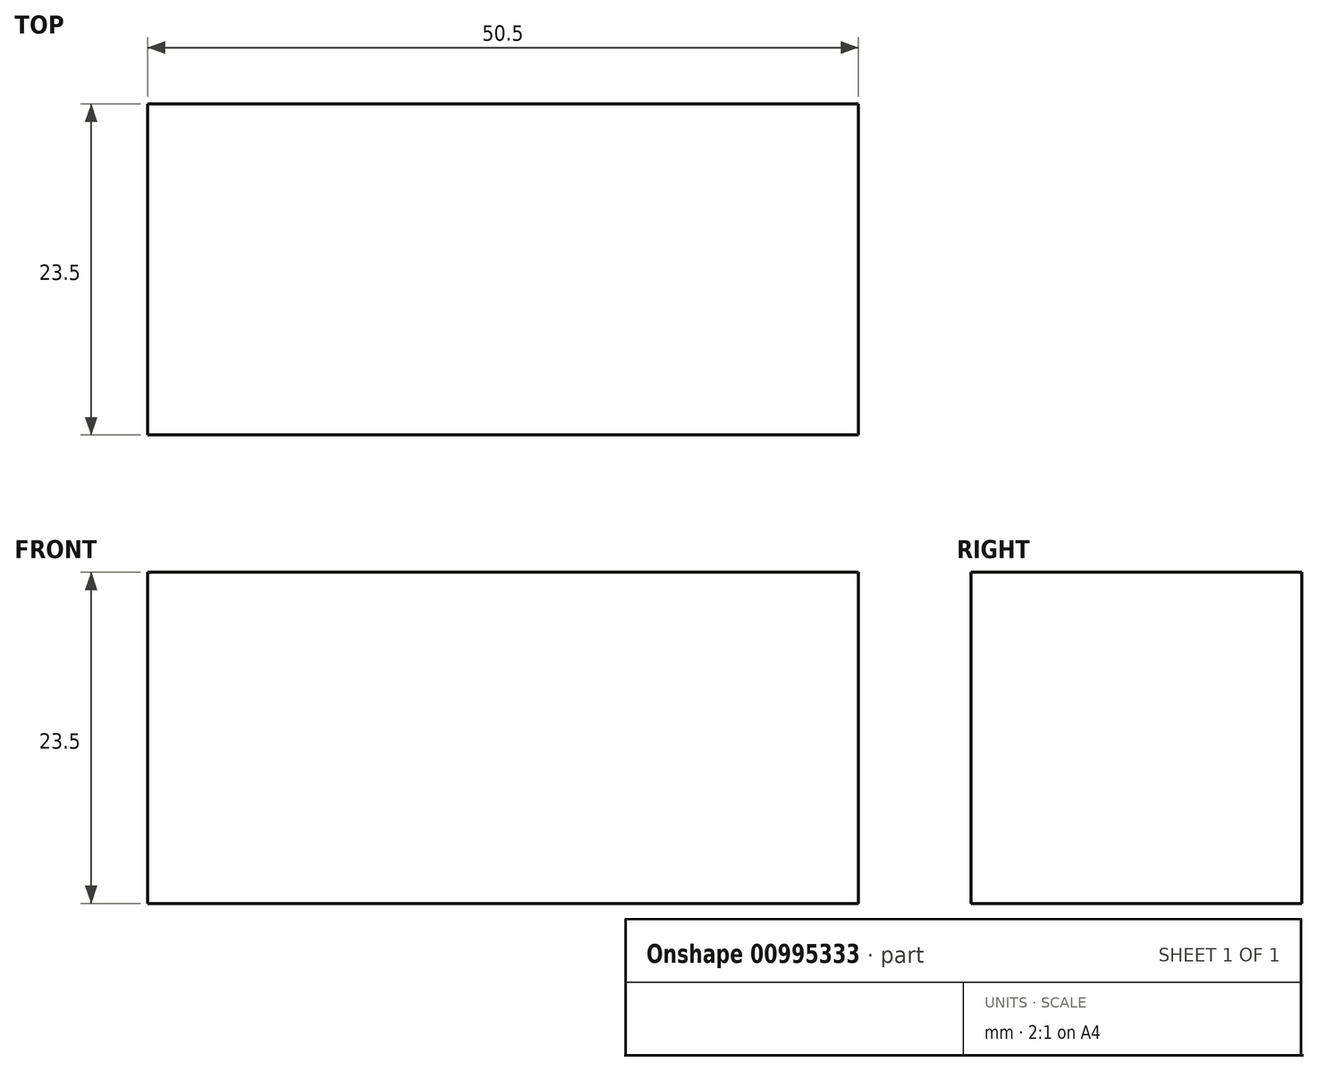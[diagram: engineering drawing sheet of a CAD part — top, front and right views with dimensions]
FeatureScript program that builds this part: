
annotation { "Feature Type Name" : "Feature", "Feature Type Description" : "" }
export const myFeature = defineFeature(function(context is Context, id is Id, definition is map)
    precondition{}
    {
        {
            var Q0;
            Q0=qCreatedBy(makeId("Top.planeOp"),FACE);
            var sketch = newSketch(context, id + "F0", { "sketchPlane" : qUnion([Q0])});
            skLineSegment(sketch, "E0.bottom", {"start": v(25.25, 11.75) * mm, "end": v(-25.25, 11.75) * mm});
            skLineSegment(sketch, "E0.top", {"start": v(25.25, -11.75) * mm, "end": v(-25.25, -11.75) * mm});
            skLineSegment(sketch, "E0.left", {"start": v(25.25, 11.75) * mm, "end": v(25.25, -11.75) * mm});
            skLineSegment(sketch, "E0.right", {"start": v(-25.25, 11.75) * mm, "end": v(-25.25, -11.75) * mm});
            skPoint(sketch, "E0.middle", {"position": v(0, 0) * mm});
            skSolve(sketch);
        }
        {
            var Q0;
            Q0 = qSketchRegion(id + "F0", true);
            extrude(context, id + "F1", {"entities" : qUnion([Q0]), "depth" : 23.5 * mm, "offsetDistance" : 25 * mm});
        }
    });
